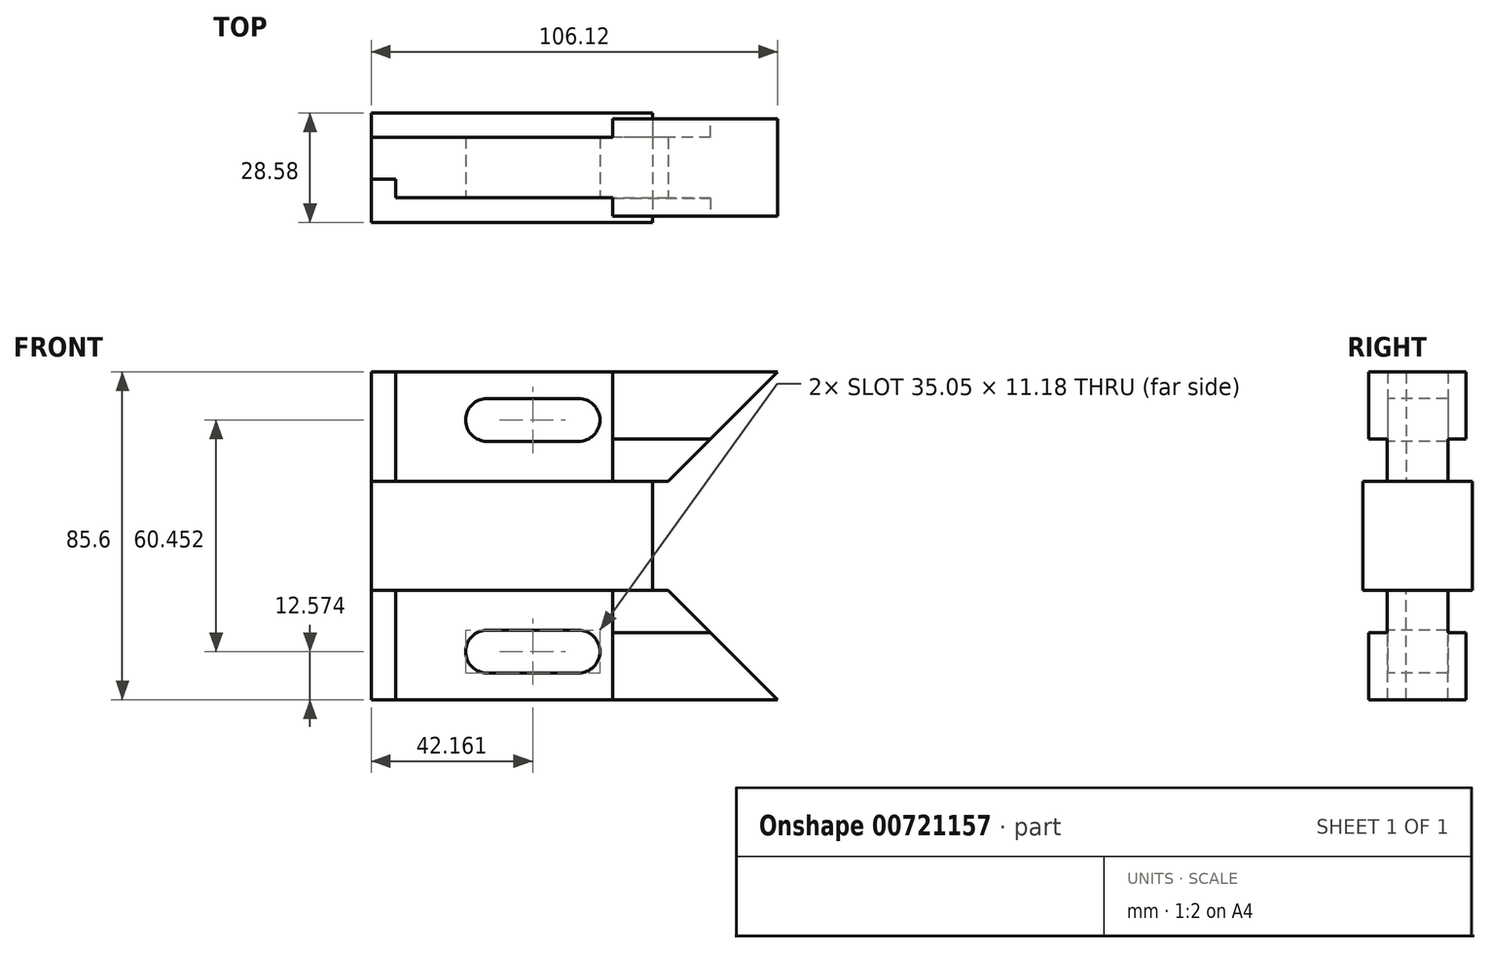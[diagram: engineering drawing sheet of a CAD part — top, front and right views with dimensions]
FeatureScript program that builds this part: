
annotation { "Feature Type Name" : "Feature", "Feature Type Description" : "" }
export const myFeature = defineFeature(function(context is Context, id is Id, definition is map)
    precondition{}
    {
        {
            var Q0;
            Q0=qCreatedBy(makeId("Top.planeOp"),FACE);
            var sketch = newSketch(context, id + "F0", { "sketchPlane" : qUnion([Q0])});
            skLineSegment(sketch, "E0.bottom", {"start": v(36.7, 14.29) * mm, "end": v(-36.7, 14.29) * mm});
            skLineSegment(sketch, "E0.top", {"start": v(36.7, -14.29) * mm, "end": v(-36.7, -14.29) * mm});
            skLineSegment(sketch, "E0.left", {"start": v(36.7, 14.29) * mm, "end": v(36.7, -14.29) * mm});
            skLineSegment(sketch, "E0.right", {"start": v(-36.7, 14.29) * mm, "end": v(-36.7, -14.29) * mm});
            skPoint(sketch, "E0.middle", {"position": v(0, 0) * mm});
            skSolve(sketch);
        }
        {
            var Q0;
            Q0=makeQuery(id+"F0.imprint","IMPRINT",FACE,{"disambiguationData":[TD([[makeQuery(id+"F0.imprint","IMPRINT",EDGE,{"derivedFrom":sQuery(id+"F0.wireOp",EDGE,"E0.bottom")}),1.0]])]});
            extrude(context, id + "F1", {"entities" : qUnion([Q0]), "endBound" : BoundingType.SYMMETRIC, "depth" : 28.45 * mm, "offsetDistance" : 25.4 * mm});
        }
        {
            var Q0;
            Q0=makeQuery(id+"F1.opExtrude","CAP_FACE",FACE,{"disambiguationData":[OSD([sQuery(id+"F0.wireOp",EDGE,"E0.bottom"),sQuery(id+"F0.wireOp",EDGE,"E0.top"),sQuery(id+"F0.wireOp",EDGE,"E0.left"),sQuery(id+"F0.wireOp",EDGE,"E0.right")])],"isStart":false});
            var sketch = newSketch(context, id + "F2", { "sketchPlane" : qUnion([Q0])});
            skLineSegment(sketch, "E1", {"start": v(-36.7, 7.94) * mm, "end": v(26.32, 7.94) * mm});
            skLineSegment(sketch, "E2", {"start": v(26.32, -7.81) * mm, "end": v(-30.35, -7.81) * mm});
            skLineSegment(sketch, "E3", {"start": v(-30.35, -7.81) * mm, "end": v(-30.35, -2.98) * mm});
            skLineSegment(sketch, "E4", {"start": v(-30.35, -2.98) * mm, "end": v(-36.7, -2.98) * mm});
            skLineSegment(sketch, "E5", {"start": v(-36.7, 7.94) * mm, "end": v(-36.7, -2.98) * mm});
            skLineSegment(sketch, "E6", {"start": v(69.42, 0) * mm, "end": v(69.42, 12.7) * mm});
            skLineSegment(sketch, "E7", {"start": v(69.42, 12.7) * mm, "end": v(26.32, 12.7) * mm});
            skLineSegment(sketch, "E8", {"start": v(26.32, 12.7) * mm, "end": v(26.32, 7.94) * mm});
            skLineSegment(sketch, "E9", {"start": v(69.42, 0) * mm, "end": v(69.42, -12.7) * mm});
            skLineSegment(sketch, "E10", {"start": v(69.42, -12.7) * mm, "end": v(26.32, -12.7) * mm});
            skLineSegment(sketch, "E11", {"start": v(26.32, -12.7) * mm, "end": v(26.32, -7.81) * mm});
            skSolve(sketch);
        }
        {
            var Q0;
            Q0=makeQuery(id+"F2.imprint","IMPRINT",FACE,{"disambiguationData":[TD([[makeQuery(id+"F2.imprint","IMPRINT",EDGE,{"derivedFrom":sQuery(id+"F2.wireOp",EDGE,"E1")}),-1.0]])]});
            var Q1;
            {var subQ2=sQuery(id+"F2.wireOp",EDGE,"E6");Q1=makeQuery(id+"F2.imprint","IMPRINT",FACE,{"disambiguationData":[TD([[makeQuery(id+"F2.imprint","IMPRINT",EDGE,{"derivedFrom":subQ2}),1.0]])]});}
            extrude(context, id + "F3", {"entities" : qUnion([Q0, Q1]), "operationType" : NewBodyOperationType.ADD, "depth" : 28.57 * mm, "offsetDistance" : 25.4 * mm});
        }
        {
            var Q0;
            Q0=makeQuery(id+"F3.opExtrude","SWEPT_FACE",FACE,{"disambiguationData":[OSD([sQuery(id+"F2.wireOp",EDGE,"E10")])]});
            var sketch = newSketch(context, id + "F4", { "sketchPlane" : qUnion([Q0])});
            skLineSegment(sketch, "E12", {"start": v(69.42, 42.8) * mm, "end": v(40.84, 14.22) * mm});
            skSolve(sketch);
        }
        {
            var Q0;
            {var subQ0=sQuery(id+"F4.wireOp",EDGE,"E12");Q0=makeQuery(id+"F4.imprint","IMPRINT",FACE,{"disambiguationData":[TD([[makeQuery(id+"F4.imprint","IMPRINT",EDGE,{"derivedFrom":subQ0}),1.0]])]});}
            extrude(context, id + "F5", {"entities" : qUnion([Q0]), "operationType" : NewBodyOperationType.REMOVE, "oppositeDirection" : true, "depth" : 127 * mm, "offsetDistance" : 25.4 * mm});
        }
        {
            var Q0;
            Q0=makeQuery(id+"F1.opExtrude","SWEPT_BODY",BODY,{"disambiguationData":[OSD([sQuery(id+"F0.wireOp",EDGE,"E0.bottom"),sQuery(id+"F0.wireOp",EDGE,"E0.top"),sQuery(id+"F0.wireOp",EDGE,"E0.left"),sQuery(id+"F0.wireOp",EDGE,"E0.right")])]});
            var Q1;
            Q1=qCreatedBy(makeId("Top.planeOp"),FACE);
            mirror(context, id + "F6", {"operationType" : NewBodyOperationType.ADD, "entities" : qUnion([Q0]), "mirrorPlane" : qUnion([Q1])});
        }
        {
            var Q0;
            Q0=makeQuery(id+"F3.opExtrude","SWEPT_FACE",FACE,{"disambiguationData":[OSD([sQuery(id+"F2.wireOp",EDGE,"E10")])]});
            var sketch = newSketch(context, id + "F7", { "sketchPlane" : qUnion([Q0])});
            skLineSegment(sketch, "E13", {"start": v(32.9, 25.27) * mm, "end": v(51.9, 25.27) * mm});
            skLineSegment(sketch, "E14", {"start": v(32.9, 25.27) * mm, "end": v(26.32, 25.27) * mm});
            skPoint(sketch, "E14.endSnap0", {"position": v(26.32, 28.51) * mm});
            skPoint(sketch, "E15.start.orphan", {"position": v(32.9, 42.8) * mm});
            skSolve(sketch);
        }
        {
            var Q0;
            Q0=makeQuery(id+"F6.opPattern","COPY",FACE,{"derivedFrom":makeQuery(id+"F3.opExtrude","SWEPT_FACE",FACE,{"disambiguationData":[OSD([sQuery(id+"F2.wireOp",EDGE,"E10")])]}),"instanceName":"1"});
            var sketch = newSketch(context, id + "F8", { "sketchPlane" : qUnion([Q0])});
            skLineSegment(sketch, "E16", {"start": v(26.32, -25.27) * mm, "end": v(51.9, -25.27) * mm});
            skSolve(sketch);
        }
        {
            var Q0;
            {var subQ7=sQuery(id+"F7.wireOp",EDGE,"E13");Q0=makeQuery(id+"F7.imprint","IMPRINT",FACE,{"disambiguationData":[TD([[makeQuery(id+"F7.imprint","IMPRINT",EDGE,{"derivedFrom":subQ7}),-1.0]])]});}
            var Q1;
            {var subQ7=sQuery(id+"F8.wireOp",EDGE,"E16");Q1=makeQuery(id+"F8.imprint","IMPRINT",FACE,{"disambiguationData":[TD([[makeQuery(id+"F8.imprint","IMPRINT",EDGE,{"derivedFrom":subQ7}),1.0]])]});}
            extrude(context, id + "F9", {"entities" : qUnion([Q0, Q1]), "operationType" : NewBodyOperationType.REMOVE, "oppositeDirection" : true, "depth" : 4.78 * mm, "offsetDistance" : 25.4 * mm});
        }
        {
            var Q0;
            Q0=makeQuery(id+"F6.opPattern","COPY",FACE,{"derivedFrom":makeQuery(id+"F3.opExtrude","SWEPT_FACE",FACE,{"disambiguationData":[OSD([sQuery(id+"F2.wireOp",EDGE,"E7")])]}),"instanceName":"1"});
            var sketch = newSketch(context, id + "F10", { "sketchPlane" : qUnion([Q0])});
            skLineSegment(sketch, "E17", {"start": v(-51.9, -25.27) * mm, "end": v(-26.32, -25.27) * mm});
            skSolve(sketch);
        }
        {
            var Q0;
            {var subQ7=sQuery(id+"F10.wireOp",EDGE,"E17");Q0=makeQuery(id+"F10.imprint","IMPRINT",FACE,{"disambiguationData":[TD([[makeQuery(id+"F10.imprint","IMPRINT",EDGE,{"derivedFrom":subQ7}),1.0]])]});}
            extrude(context, id + "F11", {"entities" : qUnion([Q0]), "operationType" : NewBodyOperationType.REMOVE, "oppositeDirection" : true, "depth" : 4.78 * mm, "offsetDistance" : 25.4 * mm});
        }
        {
            var Q0;
            Q0=makeQuery(id+"F3.opExtrude","SWEPT_FACE",FACE,{"disambiguationData":[OSD([sQuery(id+"F2.wireOp",EDGE,"E7")])]});
            var sketch = newSketch(context, id + "F12", { "sketchPlane" : qUnion([Q0])});
            skLineSegment(sketch, "E18", {"start": v(-51.9, 25.27) * mm, "end": v(-26.32, 25.27) * mm});
            skSolve(sketch);
        }
        {
            var Q0;
            {var subQ7=sQuery(id+"F12.wireOp",EDGE,"E18");Q0=makeQuery(id+"F12.imprint","IMPRINT",FACE,{"disambiguationData":[TD([[makeQuery(id+"F12.imprint","IMPRINT",EDGE,{"derivedFrom":subQ7}),-1.0]])]});}
            extrude(context, id + "F13", {"entities" : qUnion([Q0]), "operationType" : NewBodyOperationType.REMOVE, "oppositeDirection" : true, "depth" : 4.78 * mm, "offsetDistance" : 25.4 * mm});
        }
        {
            var Q0;
            Q0=makeQuery(id+"F3.opExtrude","SWEPT_FACE",FACE,{"disambiguationData":[OSD([sQuery(id+"F2.wireOp",EDGE,"E2")])]});
            var sketch = newSketch(context, id + "F14", { "sketchPlane" : qUnion([Q0])});
            skLineSegment(sketch, "E19", {"start": v(-30.35, 30.23) * mm, "end": v(65.15, 30.23) * mm, "construction": true});
            skLineSegment(sketch, "E20", {"start": v(57.75, 30.23) * mm, "end": v(65.15, 30.23) * mm, "construction": true});
            skLineSegment(sketch, "E21", {"start": v(-30.35, -30.23) * mm, "end": v(65.15, -30.23) * mm, "construction": true});
            skArc(sketch, "E22", {"start": v(-6.48, -24.64) * mm, "mid": v(-12.07, -30.23) * mm, "end": v(-6.48, -35.81) * mm});
            skArc(sketch, "E23", {"start": v(17.4, -35.81) * mm, "mid": v(22.99, -30.23) * mm, "end": v(17.4, -24.64) * mm});
            skArc(sketch, "E24", {"start": v(-6.48, 35.81) * mm, "mid": v(-12.07, 30.23) * mm, "end": v(-6.48, 24.64) * mm});
            skArc(sketch, "E25", {"start": v(17.4, 24.64) * mm, "mid": v(22.99, 30.23) * mm, "end": v(17.4, 35.81) * mm});
            skLineSegment(sketch, "E26", {"start": v(-6.48, 35.81) * mm, "end": v(17.4, 35.81) * mm});
            skLineSegment(sketch, "E27", {"start": v(17.4, 24.64) * mm, "end": v(-6.48, 24.64) * mm});
            skLineSegment(sketch, "E28", {"start": v(-6.48, -24.64) * mm, "end": v(17.4, -24.64) * mm});
            skLineSegment(sketch, "E29", {"start": v(17.4, -35.81) * mm, "end": v(-6.48, -35.81) * mm});
            skSolve(sketch);
        }
        {
            var Q0;
            Q0=makeQuery(id+"F14.imprint","IMPRINT",FACE,{"disambiguationData":[TD([[makeQuery(id+"F14.imprint","IMPRINT",EDGE,{"derivedFrom":sQuery(id+"F14.wireOp",EDGE,"E24")}),1.0]])]});
            var Q1;
            Q1=makeQuery(id+"F14.imprint","IMPRINT",FACE,{"disambiguationData":[TD([[makeQuery(id+"F14.imprint","IMPRINT",EDGE,{"derivedFrom":sQuery(id+"F14.wireOp",EDGE,"E22")}),1.0]])]});
            extrude(context, id + "F15", {"entities" : qUnion([Q0, Q1]), "operationType" : NewBodyOperationType.REMOVE, "oppositeDirection" : true, "depth" : 25.4 * mm, "offsetDistance" : 25.4 * mm});
        }
    });
